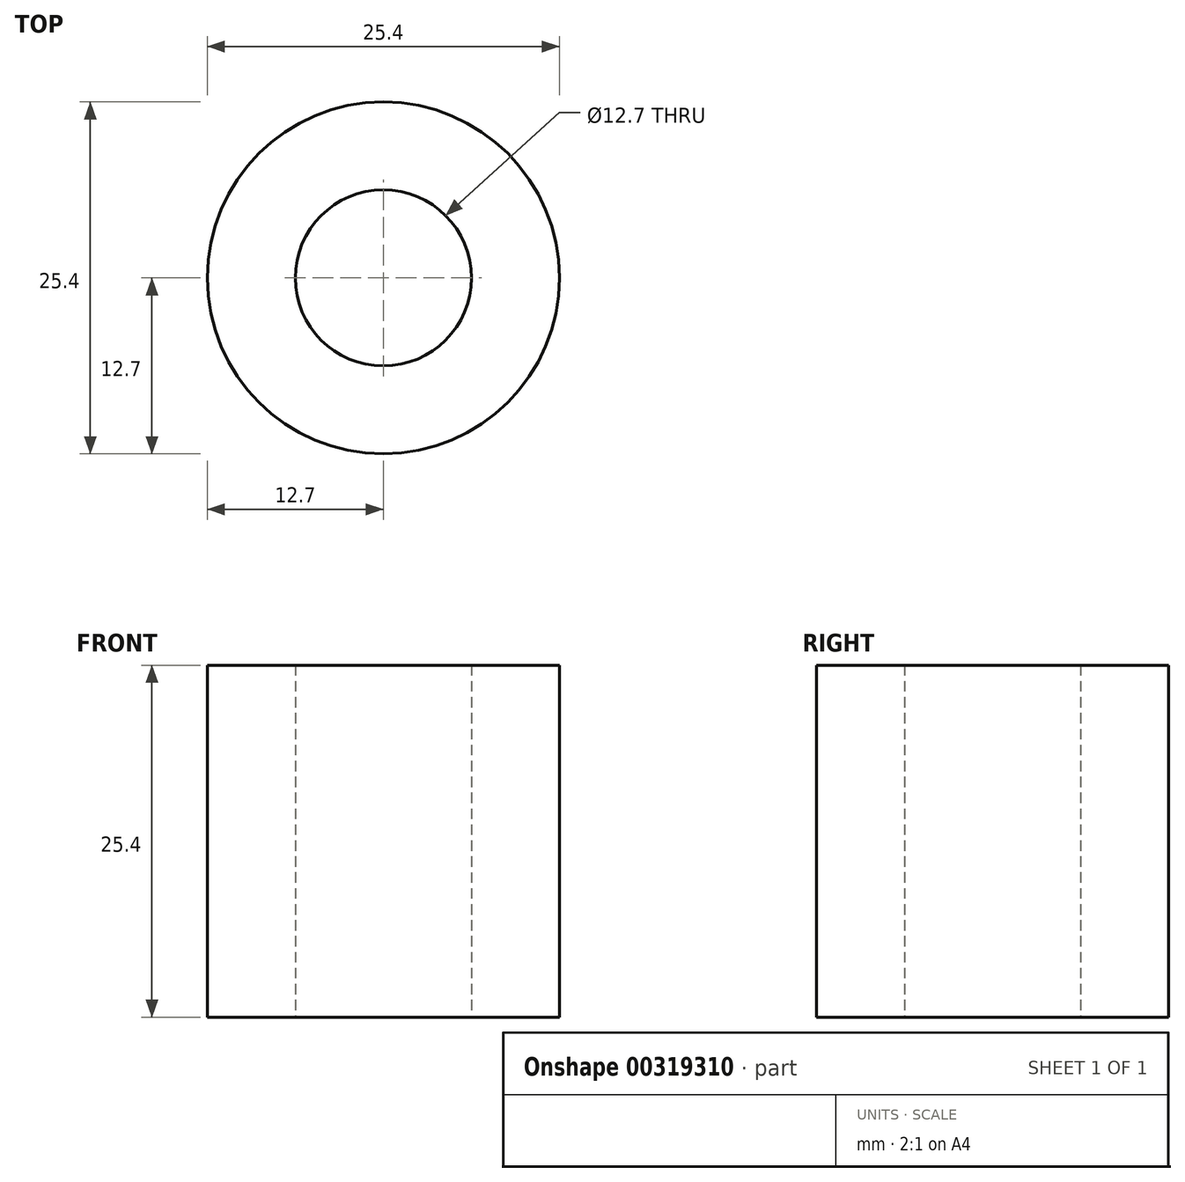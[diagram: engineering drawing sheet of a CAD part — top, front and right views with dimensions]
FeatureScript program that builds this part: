
annotation { "Feature Type Name" : "Feature", "Feature Type Description" : "" }
export const myFeature = defineFeature(function(context is Context, id is Id, definition is map)
    precondition{}
    {
        {
            var Q0;
            Q0=qCreatedBy(makeId("Top.planeOp"),FACE);
            var sketch = newSketch(context, id + "F0", { "sketchPlane" : qUnion([Q0])});
            skCircle(sketch, "E0", {"center": v(0, 0) * mm, "radius": 12.7 * mm});
            skCircle(sketch, "E1", {"center": v(0, 0) * mm, "radius": 6.35 * mm});
            skSolve(sketch);
        }
        {
            var Q0;
            Q0 = qSketchRegion(id + "F0", true);
            extrude(context, id + "F1", {"entities" : qUnion([Q0]), "endBound" : BoundingType.SYMMETRIC, "depth" : 25.4 * mm});
        }
    });
